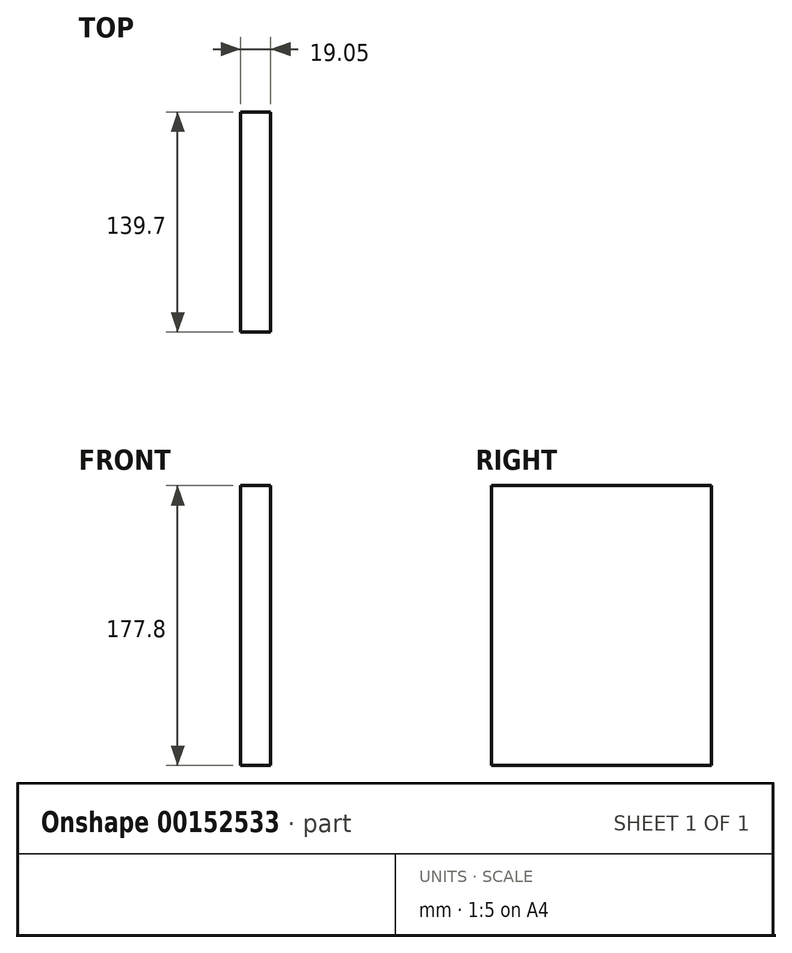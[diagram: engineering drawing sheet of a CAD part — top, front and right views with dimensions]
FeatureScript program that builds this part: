
annotation { "Feature Type Name" : "Feature", "Feature Type Description" : "" }
export const myFeature = defineFeature(function(context is Context, id is Id, definition is map)
    precondition{}
    {
        {
            var Q0;
            Q0=qCreatedBy(makeId("Right.planeOp"),FACE);
            var sketch = newSketch(context, id + "F0", { "sketchPlane" : qUnion([Q0])});
            skLineSegment(sketch, "E0.bottom", {"start": v(-69.85, 88.9) * mm, "end": v(69.85, 88.9) * mm});
            skLineSegment(sketch, "E0.top", {"start": v(-69.85, -88.9) * mm, "end": v(69.85, -88.9) * mm});
            skLineSegment(sketch, "E0.left", {"start": v(-69.85, 88.9) * mm, "end": v(-69.85, -88.9) * mm});
            skLineSegment(sketch, "E0.right", {"start": v(69.85, 88.9) * mm, "end": v(69.85, -88.9) * mm});
            skPoint(sketch, "E1", {"position": v(0, 88.9) * mm});
            skLineSegment(sketch, "E2", {"start": v(0, 88.9) * mm, "end": v(0, -88.9) * mm, "construction": true});
            skPoint(sketch, "E3", {"position": v(0, 0) * mm});
            skSolve(sketch);
        }
        {
            var Q0;
            Q0=makeQuery(id+"F0.imprint","IMPRINT",FACE,{"disambiguationData":[TD([[makeQuery(id+"F0.imprint","IMPRINT",EDGE,{"derivedFrom":sQuery(id+"F0.wireOp",EDGE,"E0.bottom")}),-1.0]])]});
            extrude(context, id + "F1", {"entities" : qUnion([Q0]), "depth" : 19.05 * mm});
        }
    });
